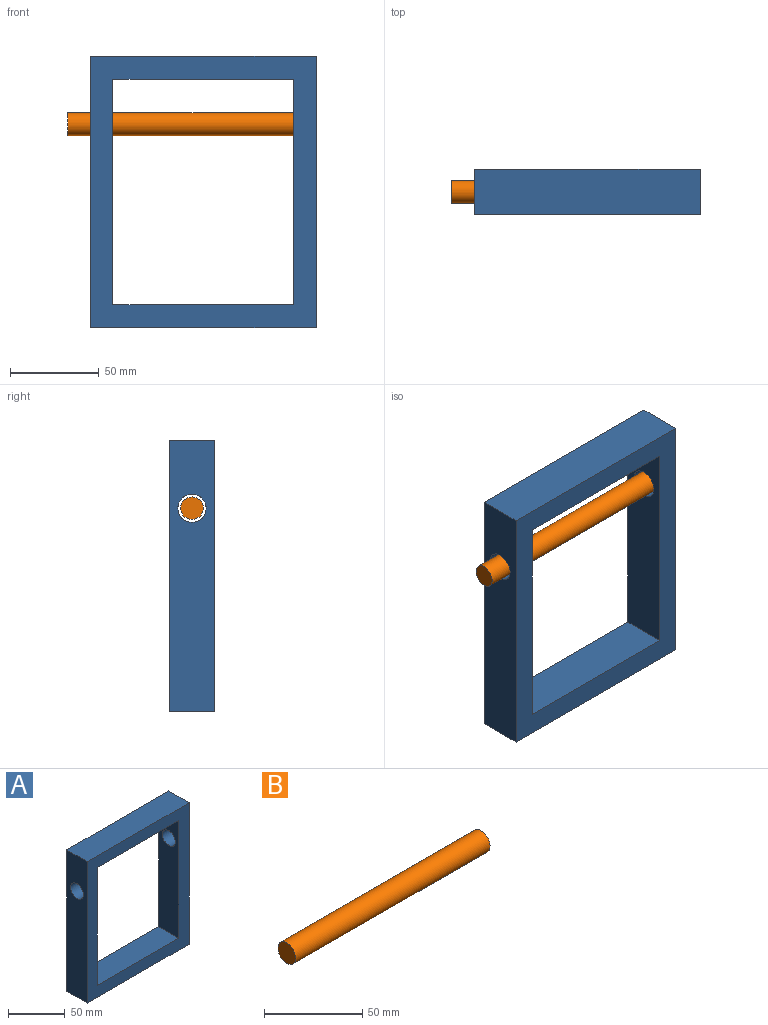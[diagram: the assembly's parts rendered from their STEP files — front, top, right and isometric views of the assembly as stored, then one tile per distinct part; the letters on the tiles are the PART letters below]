
ASSEMBLY  parts=2 mates=1
PART A: 12 faces, bbox 127x25.4x152.4 mm
  f0: plane 127x25.4mm, normal (0,0,1), area 3225.8mm2, adj f1,f7,f8,f9
  f1: plane 152.4x25.4mm, normal (-1,0,0), area 3673mm2, adj f0,f2,f8,f9,f10
  f2: plane 127x25.4mm, normal (0,0,-1), area 3225.8mm2, adj f1,f7,f8,f9
  f3: plane 101.6x25.4mm, normal (0,0,-1), area 2580.6mm2, adj f4,f6,f8,f9
  f4: plane 127x25.4mm, normal (-1,0,0), area 3027.9mm2, adj f3,f5,f8,f9,f11
  f5: plane 101.6x25.4mm, normal (0,0,1), area 2580.6mm2, adj f4,f6,f8,f9
  f6: plane 127x25.4mm, normal (1,0,0), area 3027.9mm2, adj f3,f5,f8,f9,f10
  f7: plane 152.4x25.4mm, normal (1,0,0), area 3673mm2, adj f0,f2,f8,f9,f11
  f8: plane 152.4x127mm, normal (0,-1,0), area 6451.6mm2, adj f0,f1,f2,f3,f4,f5,f6,f7
  f9: plane 152.4x127mm, normal (0,1,0), area 6451.6mm2, adj f0,f1,f2,f3,f4,f5,f6,f7
  f10: cylinder r=7.94mm len=15.88mm, axis (-1,0,0), area 633.4mm2, adj f1,f6
  f11: cylinder r=7.94mm len=15.88mm, axis (1,0,0), area 633.4mm2, adj f4,f7
PART B: 3 faces, bbox 139.7x12.7x12.7 mm
  f0: cylinder r=6.35mm len=139.7mm, axis (-1,0,0), area 5573.8mm2, adj f1,f2
  f1: plane 12.7x12.7mm, normal (1,0,0), area 126.7mm2, adj f0
  f2: plane 12.7x12.7mm, normal (-1,0,0), area 126.7mm2, adj f0
PLACE A t=(14.92,6.81,-36)mm
PLACE B rot(axis=(1,0,0),180deg) t=(-66.68,-5.89,-2.26)mm
MATE revolute B.f0 <-> A.f11  axis (1,0,0) through (73.02,-5.89,-2.26)mm
